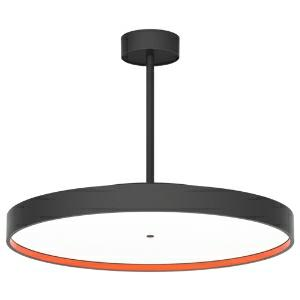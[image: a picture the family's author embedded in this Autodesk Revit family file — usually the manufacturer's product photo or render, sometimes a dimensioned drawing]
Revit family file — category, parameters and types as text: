
# Revit family: sign_diva_tube_korona_410-8430
name_source: partatom
category: Leuchten
revit_build: Autodesk Revit 2016 (Build: 20190508_0715(x64)
units: mm (PartAtom-declared; Revit-internal decimal feet)

## family parameters
Basisbauteil = Fläche
Beim Laden mit Abzugskörper schneiden = Nein
Bemaßung runder Anschluss = Durchmesser verwenden
Gemeinsam genutzt = Nein
Lichtquelle = Nein
Raumberechnungspunkt = Nein
Teiletyp = Normal

## types (1)
- 410-8430-D01-H27-S27 (1 x LED, 9097.4 lm, 2700K)
    Beschreibung = SIGN DIVA TUBE KORONA
    CIE Flux Codes = 46 76 93 80 73
    Color Rendering = 1B/80…89
    Color Temperature = 2700K
    Height = 86 mm
    Hersteller = Prolicht
    Lamp Light Flux = 9097.4 lm
    Lamp count = 1
    Lampe = 1 x LED
    Length = 570 mm
    Luminous efficacy = 98 lm/W
    ModVariant = Nein
    Modell = 410-8430
    Mounting Place = Ceiling
    Mounting Type = Pendant
    Number of Poles = 1
    OnlyDefault = Ja
    Power Factor = 1
    Product Name = SIGN DIVA TUBE KORONA
    Product group = Suspended lights
    ProductGroupID = 941
    Protection Class = Protection class
    Protection Degree = Degree of protection
    RLX_Detail_Level = 1
    RlxData = <blob elided: 228337 chars, md5=0b7f2b5c>
    Scheinlast = 68 VA
    Socket = socket
    Standby Power = 0 W
    System Light Flux = 6632 lm
    System Power = 68 W
    Typenbild = 410-8430.jpg
    Typenkommentare = DIFFUSER Opal (01),LED COLOUR DIR 2700 K (27),LED COLOUR IND 2700 K (27)
    URL = http://relux.com
    VarID = 410-8430-d01-h27-s27
    Voltage = 0 V
    Vorgabe-Ansicht = 1800 mm
    Weight = 0.00 kg
    Width = 0 mm  [stored 0 ft]

note: [stored X ft] marks values corroborated as IEEE doubles in the binary element streams (Revit-internal decimal feet)

## geometry (parser evidence)
native form markers: Blend x4, Sweep x12
no freeform markers — native parametric forms only
